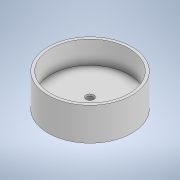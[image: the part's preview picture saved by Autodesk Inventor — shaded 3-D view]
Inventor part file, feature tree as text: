
AUTODESK INVENTOR PART (.ipt)
format: ipt  version: 2020 (Build 240168000, 168)  size: 117,760 bytes
history: native  units: mm
features: sketch x3, extrude x2, hole x1
ambient origin geometry x8: Origin, YZ Plane, XZ Plane, XY Plane, X Axis, Y Axis, Z Axis, Center Point
bodies: Solid1 (feature_tree)
feature tree (6):
  extrude  "Extrusion1"  Depth=9.0mm TaperAngle=0.0deg
  extrude  "Extrusion2"  Depth=20.0mm TaperAngle=0.0deg
  hole  "Hole1"  [1 undecoded]
  sketch  "Sketch1"  dims[d0=74.0mm d1=9.0mm d2=0.0mm]
  sketch  "Sketch2"  dims[d3=2.5mm d4=20.0mm d5=0.0mm]
  sketch  "Sketch3"  dims[d6=5.9mm d7=6.0mm d8=7.0mm d9=2.0mm d10=45.0deg d11=8.5mm d12=0.0mm]
note: 1 required parameter value undecoded (feature->parameter linkage not recoverable at this tier; creation-order binding heuristic only, values carry confidence <= 0.55)
